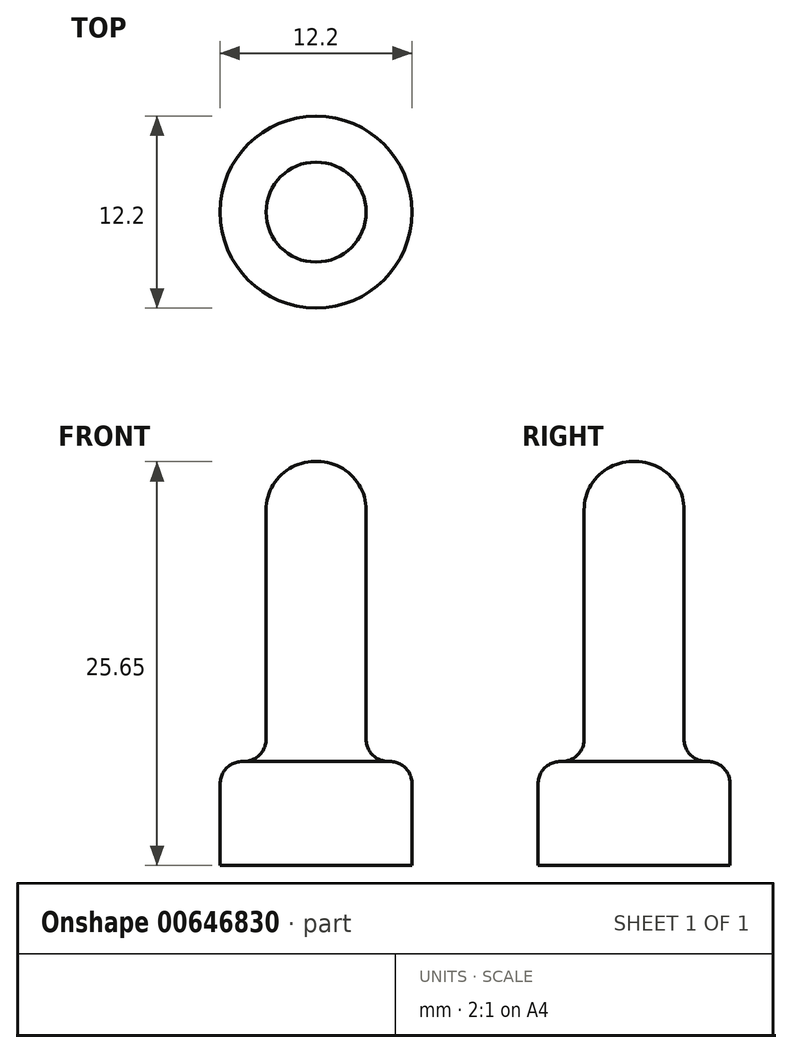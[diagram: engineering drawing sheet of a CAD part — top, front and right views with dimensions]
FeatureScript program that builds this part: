
annotation { "Feature Type Name" : "Feature", "Feature Type Description" : "" }
export const myFeature = defineFeature(function(context is Context, id is Id, definition is map)
    precondition{}
    {
        {
            var Q0;
            Q0=qCreatedBy(makeId("Top.planeOp"),FACE);
            var sketch = newSketch(context, id + "F0", { "sketchPlane" : qUnion([Q0])});
            skCircle(sketch, "E0", {"center": v(0, 0) * mm, "radius": 6.1 * mm});
            skSolve(sketch);
        }
        {
            var Q0;
            Q0 = qSketchRegion(id + "F0", true);
            extrude(context, id + "F1", {"entities" : qUnion([Q0]), "depth" : 6.6 * mm, "offsetDistance" : 25.4 * mm});
        }
        {
            var Q0;
            Q0=makeQuery(id+"F1.opExtrude","CAP_FACE",FACE,{"disambiguationData":[OSD([sQuery(id+"F0.wireOp",EDGE,"E0")])],"isStart":false});
            var sketch = newSketch(context, id + "F2", { "sketchPlane" : qUnion([Q0])});
            skCircle(sketch, "E1", {"center": v(0, 0) * mm, "radius": 3.18 * mm});
            skSolve(sketch);
        }
        {
            var Q0;
            Q0 = qSketchRegion(id + "F2", true);
            extrude(context, id + "F3", {"entities" : qUnion([Q0]), "operationType" : NewBodyOperationType.ADD, "depth" : 19.05 * mm, "offsetDistance" : 25.4 * mm});
        }
        {
            var Q0;
            Q0=makeQuery(id+"F1.opExtrude","CAP_FACE",FACE,{"disambiguationData":[OSD([sQuery(id+"F0.wireOp",EDGE,"E0")])],"isStart":false});
            fillet(context, id + "F4", {"entities" : qUnion([Q0]), "radius" : 1.41 * mm, "tangentPropagation" : true, "allowEdgeOverflow" : false});
        }
        {
            var Q0;
            Q0=makeQuery(id+"F3.opExtrude","SWEPT_FACE",FACE,{"disambiguationData":[OSD([sQuery(id+"F2.wireOp",EDGE,"E1")])]});
            var Q1;
            Q1=makeQuery(id+"F3.opExtrude","CAP_FACE",FACE,{"disambiguationData":[OSD([sQuery(id+"F2.wireOp",EDGE,"E1")])],"isStart":false});
            fillet(context, id + "F5", {"entities" : qUnion([Q0, Q1]), "radius" : 3.07 * mm, "tangentPropagation" : true, "allowEdgeOverflow" : false});
        }
    });
